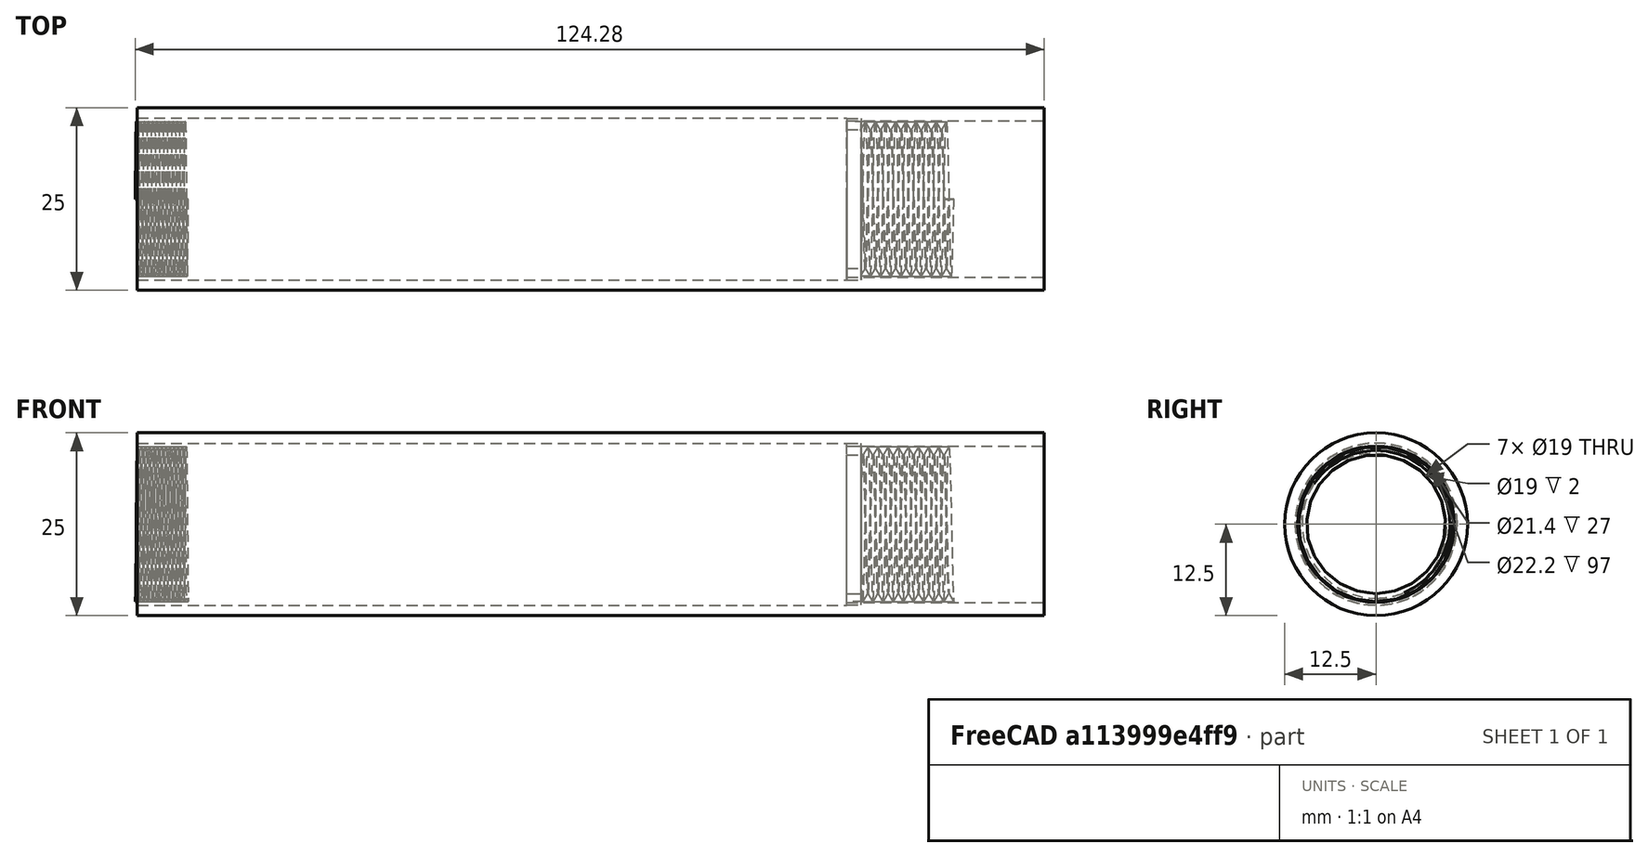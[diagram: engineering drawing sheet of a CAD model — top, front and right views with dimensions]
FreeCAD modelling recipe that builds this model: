
FCSTD DOCUMENT  (FreeCAD 0.17R13541 (Git))
Label: ERG-T-02-BH-01
License: All rights reserved
LicenseURL: http://en.wikipedia.org/wiki/All_rights_reserved
objects: Part::Cylinder×6, Part::Cut×4, Part::Helix×3, Sketcher::SketchObject×2, Part::Sweep×2, Part::MultiFuse×1
note: 18 computed .brp shape members not serialized (recipe doc carries the construction recipe); baked Part::Feature solids carry a one-line shape summary decoded from their .brp

FEATURE [Sketcher::SketchObject] Sketch007  label="T006"
  Placement = pos=(157,0,-10.6) rot=(1,0,0;1.5708rad)
  sketch-geometry (3):
    g0: LineSegment StartX=0.00120621 StartY=1.19996 StartZ=0 EndX=-0.691594 EndY=0 EndZ=0
    g1: LineSegment StartX=0.694006 StartY=0 StartZ=0 EndX=0.00120621 EndY=1.19996 EndZ=0
    g2: LineSegment StartX=-0.691594 StartY=0 StartZ=0 EndX=0.694006 EndY=0 EndZ=0
  constraints (8):
    c: PointOnObject(g1,g-1)
    c: Coincident(g1,g0)
    c: Coincident(g2,g0)
    c: Coincident(g2,g1)
    c: Horizontal(g2)
    c: Angle(g2,g0) = 1.0472
    c: Angle(g1,g2) = 1.0472
    c: Distance(g0,g0) = 1.3856
FEATURE [Part::Cylinder] Cylinder004  label="Cylinder002"
  Angle = 360
  AttacherType = Attacher::AttachEngine3D
  Height = 27
  Placement = pos=(171,0,0) rot=(0,1,0;1.5708rad)
  Radius = 10.7
FEATURE [Part::Helix] Helix010
  Angle = 35.82
  AttacherType = Attacher::AttachEngine3D
  Height = 1.3856
  LocalCoord = 0
  Pitch = 1.3856
  Placement = pos=(170.856,0,0) rot=(0,1,0;1.5708rad)
  Radius = 9.5
  Style = 1
FEATURE [Part::Cylinder] Cylinder003  label="Cylinder001"
  Angle = 360
  AttacherType = Attacher::AttachEngine3D
  Height = 97
  Placement = pos=(74,0,0) rot=(0,1,0;1.5708rad)
  Radius = 11.1
FEATURE [Part::Cylinder] Cylinder002  label="Cylinder"
  Angle = 360
  AttacherType = Attacher::AttachEngine3D
  Height = 124
  Placement = pos=(74,0,0) rot=(0,1,0;1.5708rad)
  Radius = 12.5
FEATURE [Part::Cut] Cut001
  Base = -> Cylinder002
  Tool = -> Cylinder003
FEATURE [Part::Cylinder] Cylinder013  label="Cylinder011"
  Angle = 360
  AttacherType = Attacher::AttachEngine3D
  Height = 2
  Placement = pos=(155.5,0,0) rot=(0,1,0;1.5708rad)
  Radius = 11.05
FEATURE [Part::Helix] Helix003
  Angle = 0
  AttacherType = Attacher::AttachEngine3D
  Height = 12.47
  LocalCoord = 0
  Pitch = 1.3856
  Placement = pos=(157,0,0) rot=(0,1,0;1.5708rad)
  Radius = 9.5
  Style = 1
FEATURE [Part::Sweep] Sweep004
  Frenet = true
  Sections = -> [Sketch007]
  Solid = true
  Spine = -> Helix003
  Transition = 1
FEATURE [Part::Cylinder] Cylinder015  label="Cylinder014"
  Angle = 360
  AttacherType = Attacher::AttachEngine3D
  Height = 25
  Placement = pos=(150,0,0) rot=(0,1,0;1.5708rad)
  Radius = 9.5
FEATURE [Part::Cut] Cut006
  Base = -> Sweep004
  Tool = -> Cylinder015
FEATURE [Part::Cylinder] Cylinder014  label="Cylinder013"
  Angle = 360
  AttacherType = Attacher::AttachEngine3D
  Height = 2
  Placement = pos=(155.5,0,0) rot=(0,1,0;1.5708rad)
  Radius = 9.5
FEATURE [Part::Cut] Cut004
  Base = -> Cylinder013
  Tool = -> Cylinder014
FEATURE [Part::MultiFuse] Fusion001
  Placement = pos=(15.5,0,0) rot=(0,0,1;0rad)
  Shapes = -> [Cut006,Cut004]
FEATURE [Part::Cut] Cut002  label="BatteryHolder"
  Base = -> Cut001
  Tool = -> Cylinder004
FEATURE [Sketcher::SketchObject] Sketch008  label="T007"
  Placement = pos=(157,0,-10.6) rot=(1,0,0;1.5708rad)
  sketch-geometry (3):
    g0: LineSegment StartX=-4e-12 StartY=0.484108 StartZ=0 EndX=-0.2795 EndY=0 EndZ=0
    g1: LineSegment StartX=0.2795 StartY=0 StartZ=0 EndX=-4e-12 EndY=0.484108 EndZ=0
    g2: LineSegment StartX=-0.2795 StartY=0 StartZ=0 EndX=0.2795 EndY=0 EndZ=0
  constraints (9):
    c: PointOnObject(g1,g-1)
    c: Coincident(g1,g0)
    c: Coincident(g2,g0)
    c: Coincident(g2,g1)
    c: Horizontal(g2)
    c: Angle(g2,g0) = 1.0472
    c: Angle(g1,g2) = 1.0472
    c: Distance(g0,g0) = 0.559
    c: Symmetric(g0,g1,g-2)
FEATURE [Part::Helix] Helix011
  Angle = 0
  AttacherType = Attacher::AttachEngine3D
  Height = 6.708
  LocalCoord = 0
  Pitch = 0.559
  Placement = pos=(157,0,0) rot=(0,1,0;1.5708rad)
  Radius = 9.5
  Style = 1
FEATURE [Part::Sweep] Sweep005
  Frenet = true
  Placement = pos=(-83,0,0) rot=(0,0,1;0rad)
  Sections = -> [Sketch008]
  Solid = true
  Spine = -> Helix011
  Transition = 1
